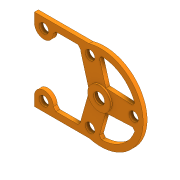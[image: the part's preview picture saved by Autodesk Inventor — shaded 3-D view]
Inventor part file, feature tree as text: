
AUTODESK INVENTOR PART (.ipt)
format: ipt  version: 2020 (Build 240168000, 168)  size: 540,672 bytes
history: native  units: in
note: dims shown in document units (in); Inventor stores cm internally (conversion verified against a paired STEP export)
features: sketch x16, extrude x15, projected_geometry x6, plane x3, fillet x2, emboss x1
ambient origin geometry x8: Origin, YZ Plane, XZ Plane, XY Plane, X Axis, Y Axis, Z Axis, Center Point
bodies: Solid1 (feature_tree)
feature tree (43):
  extrude  "Extrusion1"  Depth=0.2362in
  extrude  "Extrusion2"  Depth=0.2362in
  extrude  "Extrusion3"  Depth=0.2362in
  fillet  "Fillet1"  Radius=0.2264in
  plane  "Work Plane1"
  extrude  "Extrusion4"  Depth=0.1969in
  sketch  "Sketch5"  dims[d11=0.0in d12=0.0in d13=0.0787in]
  extrude  "Extrusion5"  Depth=0.0787in
  extrude  "Extrusion6"  Depth=0.5512in
  extrude  "Extrusion7"  Depth=0.9843in
  emboss  "Emboss1"
  plane  "Work Plane2"
  extrude  "Extrusion8"  Depth=0.0197in
  extrude  "Extrusion9"  Depth=0.0197in
  extrude  "Extrusion10"  Depth=0.0787in TaperAngle=0.0deg
  extrude  "Extrusion11"  Depth=0.0394in TaperAngle=0.0deg
  plane  "Work Plane3"
  extrude  "Extrusion12"  Depth=0.3543in
  extrude  "Extrusion13"  Depth=0.3543in
  extrude  "Extrusion14"  Depth=0.4724in TaperAngle=0.0deg
  extrude  "Extrusion15"  Depth=0.0984in
  fillet  "Fillet2"  Radius=0.0984in
  sketch  "Sketch1"  dims[d0=0.1575in d1=0.2362in]
  sketch  "Sketch2"  dims[d2=0.2362in d3=0.2362in]
  sketch  "Sketch3"  dims[d4=0.2362in d5=0.2362in d6=0.2264in d7=0.0in]
  sketch  "Sketch4"  dims[d8=0.1969in d9=0.0in d10=0.1969in]
  projected_geometry  "Projected Loop1"
  sketch  "Sketch6"  dims[d14=0.5512in d15=0.5512in]
  sketch  "Sketch7"  dims[d16=0.9843in d17=0.9843in]
  sketch  "Sketch8"  dims[d18=0.0787in d19=0.0in d20=0.0197in]
  sketch  "Sketch9"  dims[d21=0.0197in d22=0.0197in]
  sketch  "Sketch10"  dims[d23=0.0in d24=0.0in d25=0.0787in d26=0.0in]
  sketch  "Sketch11"  dims[d27=0.0in d28=0.0in d29=0.0394in d30=0.0in]
  sketch  "Sketch12"  dims[d31=0.3543in d32=0.3543in]
  sketch  "Sketch13"  dims[d33=0.3543in d34=0.3543in]
  projected_geometry  "Projected Loop2"
  projected_geometry  "Projected Loop3"
  sketch  "Sketch14"  dims[d35=0.3543in d36=0.4724in d37=0.0in]
  projected_geometry  "Projected Loop4"
  sketch  "Sketch15"  dims[d38=0.315in d39=0.5512in d40=0.0984in d41=0.0in]
  projected_geometry  "Projected Loop5"
  projected_geometry  "Projected Loop6"
  sketch  "Sketch17"  dims[d42=0.0984in d43=0.0in d44=0.2362in d45=0.0394in d46=0.0in d47=-0.0984in d48=0.0in d49=0.0in d50=0.0in d51=0.0in d52=0.3937in d53=0.0in d54=0.1969in d55=0.2756in d56=0.0394in d57=0.0in d58=0.0276in]
